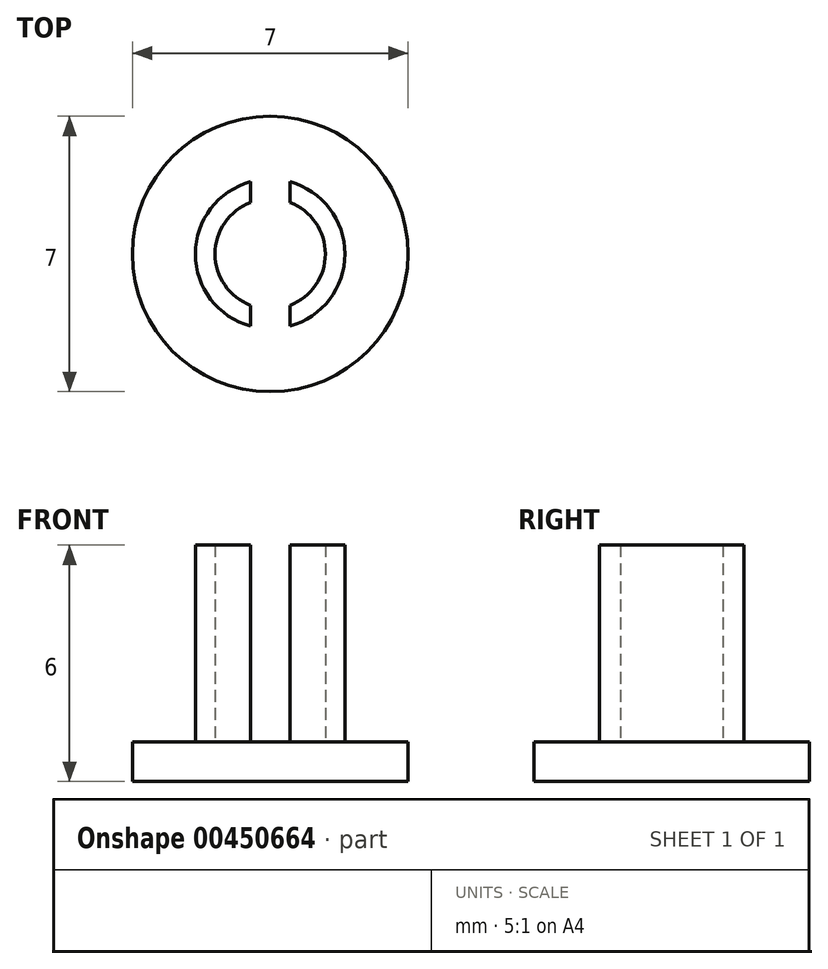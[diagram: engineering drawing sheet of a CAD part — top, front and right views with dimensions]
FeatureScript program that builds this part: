
annotation { "Feature Type Name" : "Feature", "Feature Type Description" : "" }
export const myFeature = defineFeature(function(context is Context, id is Id, definition is map)
    precondition{}
    {
        {
            var Q0;
            Q0=qCreatedBy(makeId("Top.planeOp"),FACE);
            var sketch = newSketch(context, id + "F0", { "sketchPlane" : qUnion([Q0])});
            skCircle(sketch, "E0", {"center": v(0, 0) * mm, "radius": 3.5 * mm});
            skSolve(sketch);
        }
        {
            var Q0;
            Q0 = qSketchRegion(id + "F0", true);
            extrude(context, id + "F1", {"entities" : qUnion([Q0]), "endBound" : BoundingType.SYMMETRIC, "depth" : 1 * mm});
        }
        {
            var Q0;
            Q0=makeQuery(id+"F1.opExtrude","CAP_FACE",FACE,{"disambiguationData":[OSD([sQuery(id+"F0.wireOp",EDGE,"E0")])],"isStart":false});
            var sketch = newSketch(context, id + "F2", { "sketchPlane" : qUnion([Q0])});
            skCircle(sketch, "E1", {"center": v(0, 0) * mm, "radius": 1.9 * mm});
            skCircle(sketch, "E2", {"center": v(0, 0) * mm, "radius": 1.4 * mm});
            skSolve(sketch);
        }
        {
            var Q0;
            Q0 = qSketchRegion(id + "F2", true);
            extrude(context, id + "F3", {"entities" : qUnion([Q0]), "operationType" : NewBodyOperationType.ADD, "depth" : 5 * mm});
        }
        {
            var Q0;
            Q0=makeQuery(id+"F3.opExtrude","CAP_FACE",FACE,{"disambiguationData":[OSD([sQuery(id+"F2.wireOp",EDGE,"E1"),sQuery(id+"F2.wireOp",EDGE,"E2")])],"isStart":false});
            var sketch = newSketch(context, id + "F4", { "sketchPlane" : qUnion([Q0])});
            skLineSegment(sketch, "E3.bottom", {"start": v(-0.5, 2.94) * mm, "end": v(0.5, 2.94) * mm});
            skLineSegment(sketch, "E3.top", {"start": v(-0.5, -3.52) * mm, "end": v(0.5, -3.52) * mm});
            skLineSegment(sketch, "E3.left", {"start": v(-0.5, 2.94) * mm, "end": v(-0.5, -3.52) * mm});
            skLineSegment(sketch, "E3.right", {"start": v(0.5, 2.94) * mm, "end": v(0.5, -3.52) * mm});
            skSolve(sketch);
        }
        {
            var Q0;
            Q0 = qSketchRegion(id + "F4", true);
            extrude(context, id + "F5", {"entities" : qUnion([Q0]), "operationType" : NewBodyOperationType.REMOVE, "oppositeDirection" : true, "depth" : 5 * mm});
        }
    });
